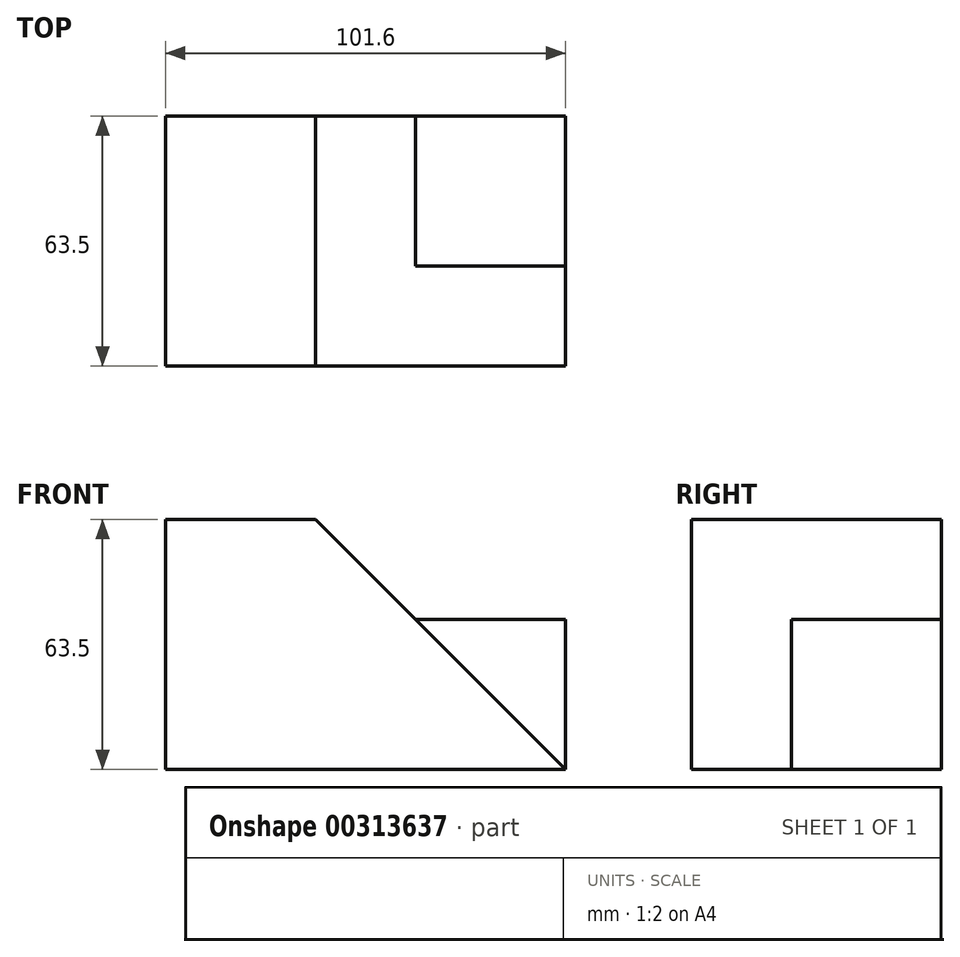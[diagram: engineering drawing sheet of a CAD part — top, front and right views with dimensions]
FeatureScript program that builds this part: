
annotation { "Feature Type Name" : "Feature", "Feature Type Description" : "" }
export const myFeature = defineFeature(function(context is Context, id is Id, definition is map)
    precondition{}
    {
        {
            var Q0;
            Q0=qCreatedBy(makeId("Front.planeOp"),FACE);
            var sketch = newSketch(context, id + "F0", { "sketchPlane" : qUnion([Q0])});
            skLineSegment(sketch, "E0", {"start": v(-38.1, -31.06) * mm, "end": v(63.5, -31.06) * mm});
            skLineSegment(sketch, "E1", {"start": v(-38.1, -31.06) * mm, "end": v(-38.1, 32.44) * mm});
            skLineSegment(sketch, "E2", {"start": v(-38.1, 32.44) * mm, "end": v(0, 32.44) * mm});
            skLineSegment(sketch, "E3", {"start": v(0, 32.44) * mm, "end": v(63.5, -31.06) * mm});
            skSolve(sketch);
        }
        {
            var Q0;
            Q0 = qSketchRegion(id + "F0", true);
            extrude(context, id + "F1", {"entities" : qUnion([Q0]), "depth" : 63.5 * mm});
        }
        {
            var Q0;
            Q0=makeQuery(id+"F1.opExtrude","CAP_FACE",FACE,{"disambiguationData":[OSD([sQuery(id+"F0.wireOp",EDGE,"E0"),sQuery(id+"F0.wireOp",EDGE,"E1"),sQuery(id+"F0.wireOp",EDGE,"E2"),sQuery(id+"F0.wireOp",EDGE,"E3")])],"isStart":true});
            var sketch = newSketch(context, id + "F2", { "sketchPlane" : qUnion([Q0])});
            skLineSegment(sketch, "E4", {"start": v(-63.5, -31.06) * mm, "end": v(-63.5, 7.04) * mm});
            skLineSegment(sketch, "E5", {"start": v(-63.5, 7.04) * mm, "end": v(-25.4, 7.04) * mm});
            skLineSegment(sketch, "E6", {"start": v(-63.5, -31.06) * mm, "end": v(-25.4, 7.04) * mm});
            skSolve(sketch);
        }
        {
            var Q0;
            Q0=makeQuery(id+"F2.imprint","IMPRINT",FACE,{"disambiguationData":[TD([[makeQuery(id+"F2.imprint","IMPRINT",EDGE,{"derivedFrom":sQuery(id+"F2.wireOp",EDGE,"E4")}),-1.0]])]});
            extrude(context, id + "F3", {"entities" : qUnion([Q0]), "operationType" : NewBodyOperationType.ADD, "oppositeDirection" : true, "depth" : 38.1 * mm});
        }
    });
